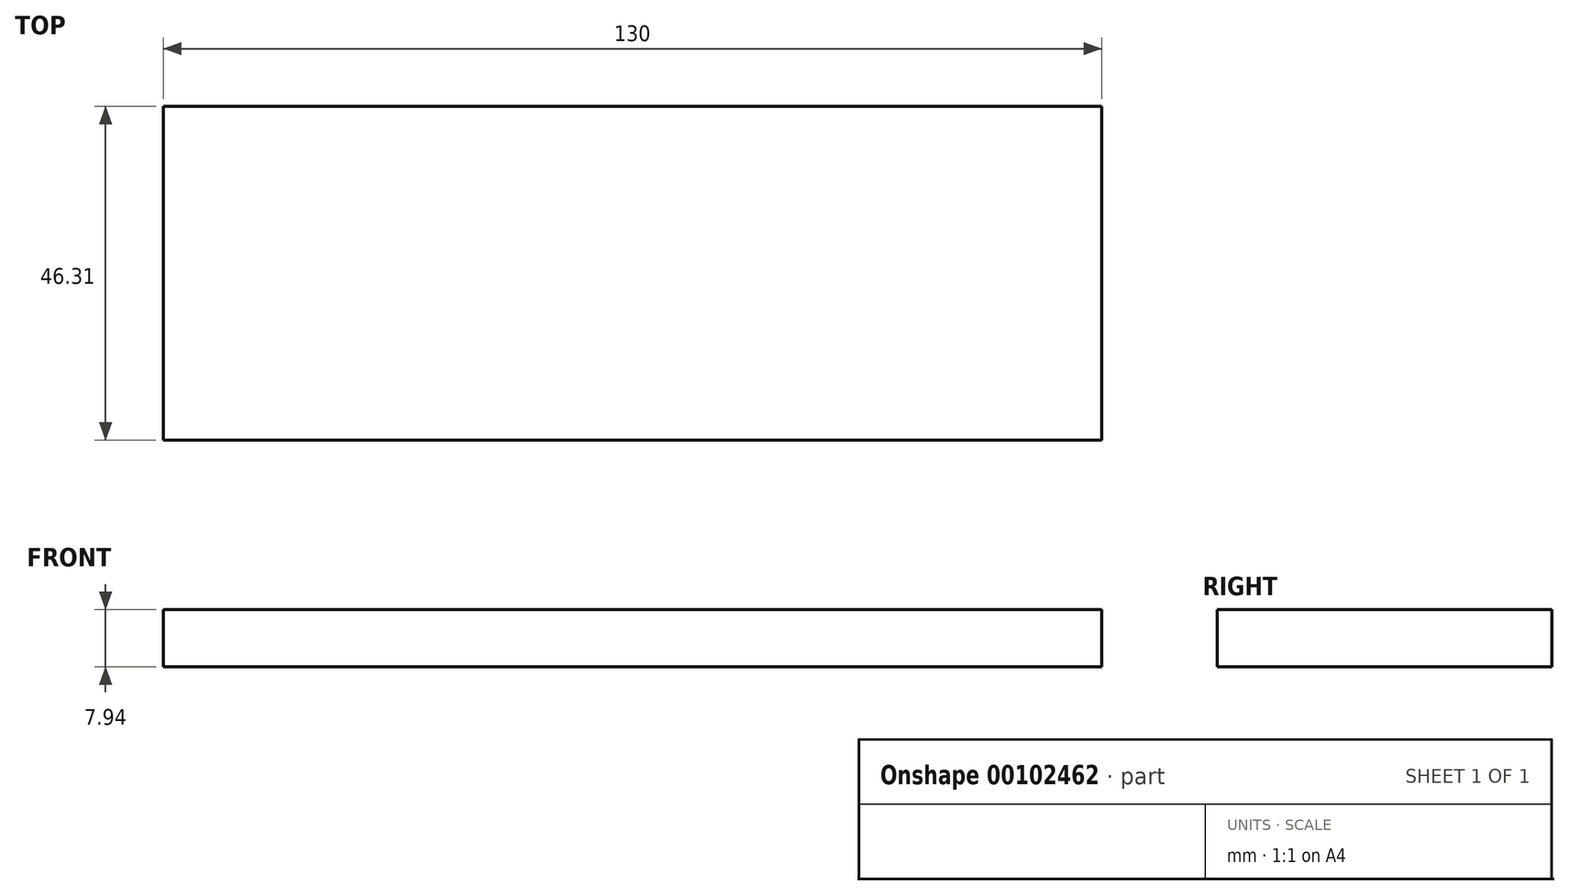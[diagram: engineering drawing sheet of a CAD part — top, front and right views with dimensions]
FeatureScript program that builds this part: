
annotation { "Feature Type Name" : "Feature", "Feature Type Description" : "" }
export const myFeature = defineFeature(function(context is Context, id is Id, definition is map)
    precondition{}
    {
        {
            var Q0;
            Q0=qCreatedBy(makeId("Top.planeOp"),FACE);
            var sketch = newSketch(context, id + "F0", { "sketchPlane" : qUnion([Q0])});
            skLineSegment(sketch, "E0.bottom", {"start": v(0, 0) * mm, "end": v(130, 0) * mm});
            skLineSegment(sketch, "E0.top", {"start": v(0, 46.31) * mm, "end": v(130, 46.31) * mm});
            skLineSegment(sketch, "E0.left", {"start": v(0, 0) * mm, "end": v(0, 46.31) * mm});
            skLineSegment(sketch, "E0.right", {"start": v(130, 0) * mm, "end": v(130, 46.31) * mm});
            skSolve(sketch);
        }
        {
            var Q0;
            Q0=qSketchRegion(id+"F0",true);
            extrude(context, id + "F1", {"entities" : qUnion([Q0]), "depth" : 7.94 * mm});
        }
    });
